# Revit family: DC_Holyoake_MEQ_LD-600SD_13
name_source: partatom
category: Air Terminals
revit_build: Autodesk Revit 2013 (Build: 20120221_2030(x64)
units: mm (PartAtom-declared; Revit-internal decimal feet)

## types (1)
- LD-600SD
    Default Elevation = 0 mm  [stored 0 ft]
    Description = Linear Bar Grille Registers with Vertical Rear Deflector Blades shall be Holyoake Model LD-600-SD with Horizontal Front Linear Bars of 3.25mm Blades at 6.35mm centres set at 0 degree deflection together with one set of Black Anodised Vertical Airfoil Individually Adjustable Deflection Blades at rear.  Linear Bar Grille Registers shall be of extruded aluminium construction to the sizes as documented. Fine line linear blades shall be mechanically expanded into machine notched mullions spaced at no greater then 300mm centres. Diffusers shall be finished in powder coat and fitted with accessories and dampers where indicated as manufactured by Holyoake
    Holyoake Product Range = Holyoake Fineline Diffusers
    Manufacturer = Holyoake
    Material Body = Holyoake-Aluminium
    Material Face = Holyoake-Aluminium
    Max Flow = 2600 L/s
    Min Flow = 29 L/s
    Model = LD-600SD
    Noise Level NC Max = 48 NC
    Noise Level NC Min = < 10 NC
    Static Pressure Max = 69.00 Pa
    Static Pressure Min = 3.00 Pa
    Type Comments = Fineline Diffuser Series LD linear bar grilles
    URL = http://www.holyoake.com

note: [stored X ft] marks values corroborated as IEEE doubles in the binary element streams (Revit-internal decimal feet)

## geometry (parser evidence)
native form markers: Blend x6, Sweep x2
no freeform markers — native parametric forms only
